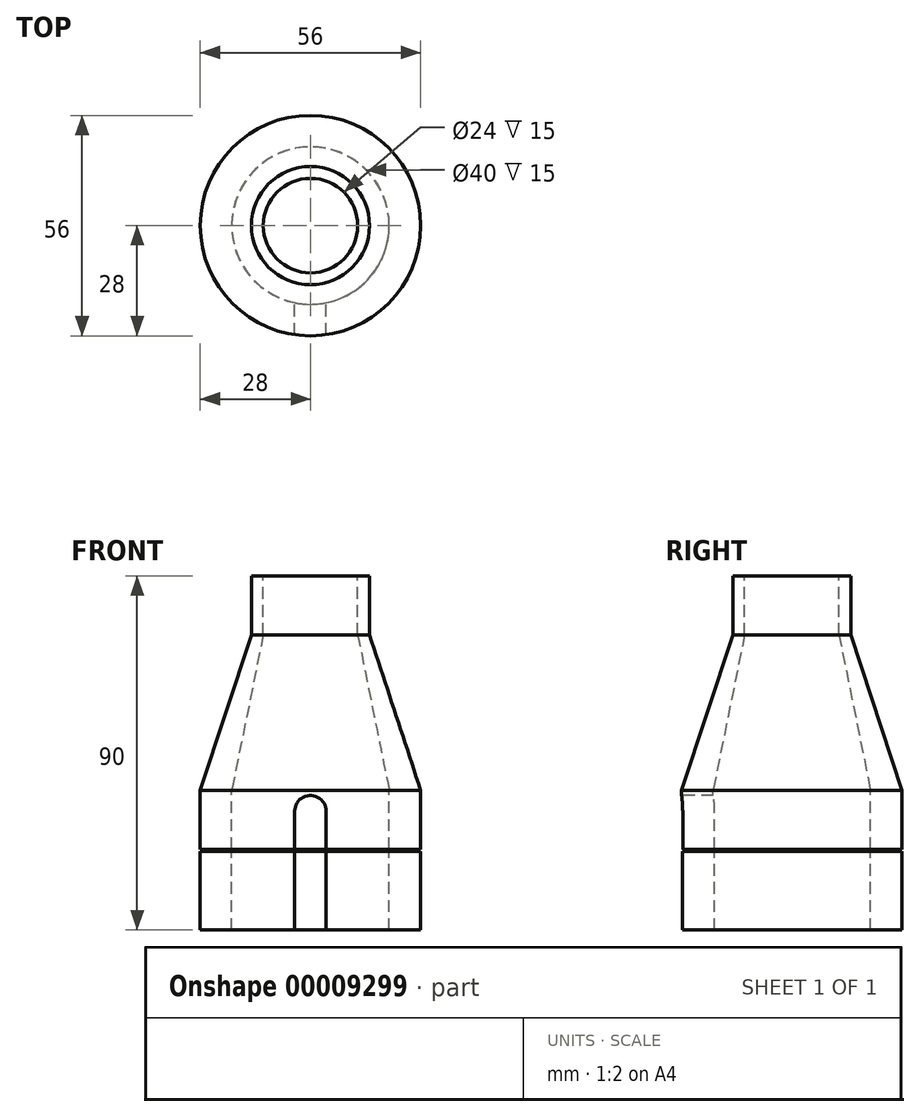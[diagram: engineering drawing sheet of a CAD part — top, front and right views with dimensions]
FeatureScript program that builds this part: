
annotation { "Feature Type Name" : "Feature", "Feature Type Description" : "" }
export const myFeature = defineFeature(function(context is Context, id is Id, definition is map)
    precondition{}
    {
        {
            var Q0;
            Q0=qCreatedBy(makeId("Top.planeOp"),FACE);
            cPlane(context, id + "F0", {"entities" : qUnion([Q0]), "cplaneType" : CPlaneType.OFFSET, "offset" : 55 * mm, "oppositeDirection" : true, "width" : 150 * mm, "height" : 150 * mm});
        }
        {
            var Q0;
            Q0=qCreatedBy(makeId("Front.planeOp"),FACE);
            cPlane(context, id + "F1", {"entities" : qUnion([Q0]), "cplaneType" : CPlaneType.OFFSET, "offset" : 35 * mm, "width" : 150 * mm, "height" : 150 * mm});
        }
        {
            var Q0;
            Q0=qCreatedBy(id+"F1.planeOp",FACE);
            var sketch = newSketch(context, id + "F2", { "sketchPlane" : qUnion([Q0])});
            skArc(sketch, "E0", {"start": v(4, -44.77) * mm, "mid": v(0, -40.77) * mm, "end": v(-4, -44.77) * mm});
            skLineSegment(sketch, "E1.top", {"start": v(-4, -55.88) * mm, "end": v(4, -55.88) * mm});
            skLineSegment(sketch, "E1.left", {"start": v(-4, -44.77) * mm, "end": v(-4, -55.88) * mm});
            skLineSegment(sketch, "E1.right", {"start": v(4, -44.77) * mm, "end": v(4, -55.88) * mm});
            skSolve(sketch);
        }
        {
            var Q0;
            Q0=qCreatedBy(makeId("Right.planeOp"),FACE);
            var sketch = newSketch(context, id + "F3", { "sketchPlane" : qUnion([Q0])});
            skLineSegment(sketch, "E2", {"start": v(12, 15) * mm, "end": v(15, 15) * mm});
            skLineSegment(sketch, "E3", {"start": v(15, 15) * mm, "end": v(15, 0) * mm});
            skLineSegment(sketch, "E4", {"start": v(15, 0) * mm, "end": v(28, -39.44) * mm});
            skLineSegment(sketch, "E5", {"start": v(28, -39.44) * mm, "end": v(28, -54.44) * mm});
            skLineSegment(sketch, "E6", {"start": v(28, -54.44) * mm, "end": v(20, -54.44) * mm});
            skLineSegment(sketch, "E7", {"start": v(20, -54.44) * mm, "end": v(20, -39.44) * mm});
            skLineSegment(sketch, "E8", {"start": v(20, -39.44) * mm, "end": v(12, 0) * mm});
            skLineSegment(sketch, "E9", {"start": v(12, 0) * mm, "end": v(12, 15) * mm});
            skLineSegment(sketch, "E10", {"start": v(0, 0) * mm, "end": v(0, -54.78) * mm, "construction": true});
            skSolve(sketch);
        }
        {
            var Q0;
            Q0=makeQuery(id+"F3.imprint","IMPRINT",FACE,{"disambiguationData":[TD([[makeQuery(id+"F3.imprint","IMPRINT",EDGE,{"derivedFrom":sQuery(id+"F3.wireOp",EDGE,"E2")}),-1.0]])]});
            var Q1;
            Q1=sQuery(id+"F3.wireOp",EDGE,"E10");
            revolve(context, id + "F4", {"entities" : qUnion([Q0]), "axis" : qUnion([Q1]), "revolveType" : RevolveType.FULL});
        }
        {
            var Q0;
            Q0=makeQuery(id+"F2.imprint","IMPRINT",FACE,{"disambiguationData":[TD([[makeQuery(id+"F2.imprint","IMPRINT",EDGE,{"derivedFrom":sQuery(id+"F2.wireOp",EDGE,"E0")}),1.0]])]});
            extrude(context, id + "F5", {"entities" : qUnion([Q0]), "operationType" : NewBodyOperationType.REMOVE, "oppositeDirection" : true, "depth" : 25 * mm});
        }
        {
            var Q0;
            Q0=qCreatedBy(id+"F0.planeOp",FACE);
            var sketch = newSketch(context, id + "F6", { "sketchPlane" : qUnion([Q0])});
            skArc(sketch, "E11", {"start": v(3.96, -19.6) * mm, "mid": v(0.03, 20) * mm, "end": v(-4.02, -19.6) * mm});
            skArc(sketch, "E12", {"start": v(3.96, -27.72) * mm, "mid": v(0.03, 28) * mm, "end": v(-4.02, -27.71) * mm});
            skLineSegment(sketch, "E13", {"start": v(-4.02, -27.71) * mm, "end": v(-4.02, -19.6) * mm});
            skLineSegment(sketch, "E14", {"start": v(3.96, -27.72) * mm, "end": v(3.96, -19.6) * mm});
            skSolve(sketch);
        }
        {
            var Q0;
            Q0=makeQuery(id+"F6.imprint","IMPRINT",FACE,{"disambiguationData":[TD([[makeQuery(id+"F6.imprint","IMPRINT",EDGE,{"derivedFrom":sQuery(id+"F6.wireOp",EDGE,"E11")}),-1.0]])]});
            extrude(context, id + "F7", {"entities" : qUnion([Q0]), "oppositeDirection" : true, "depth" : 20 * mm});
        }
    });
